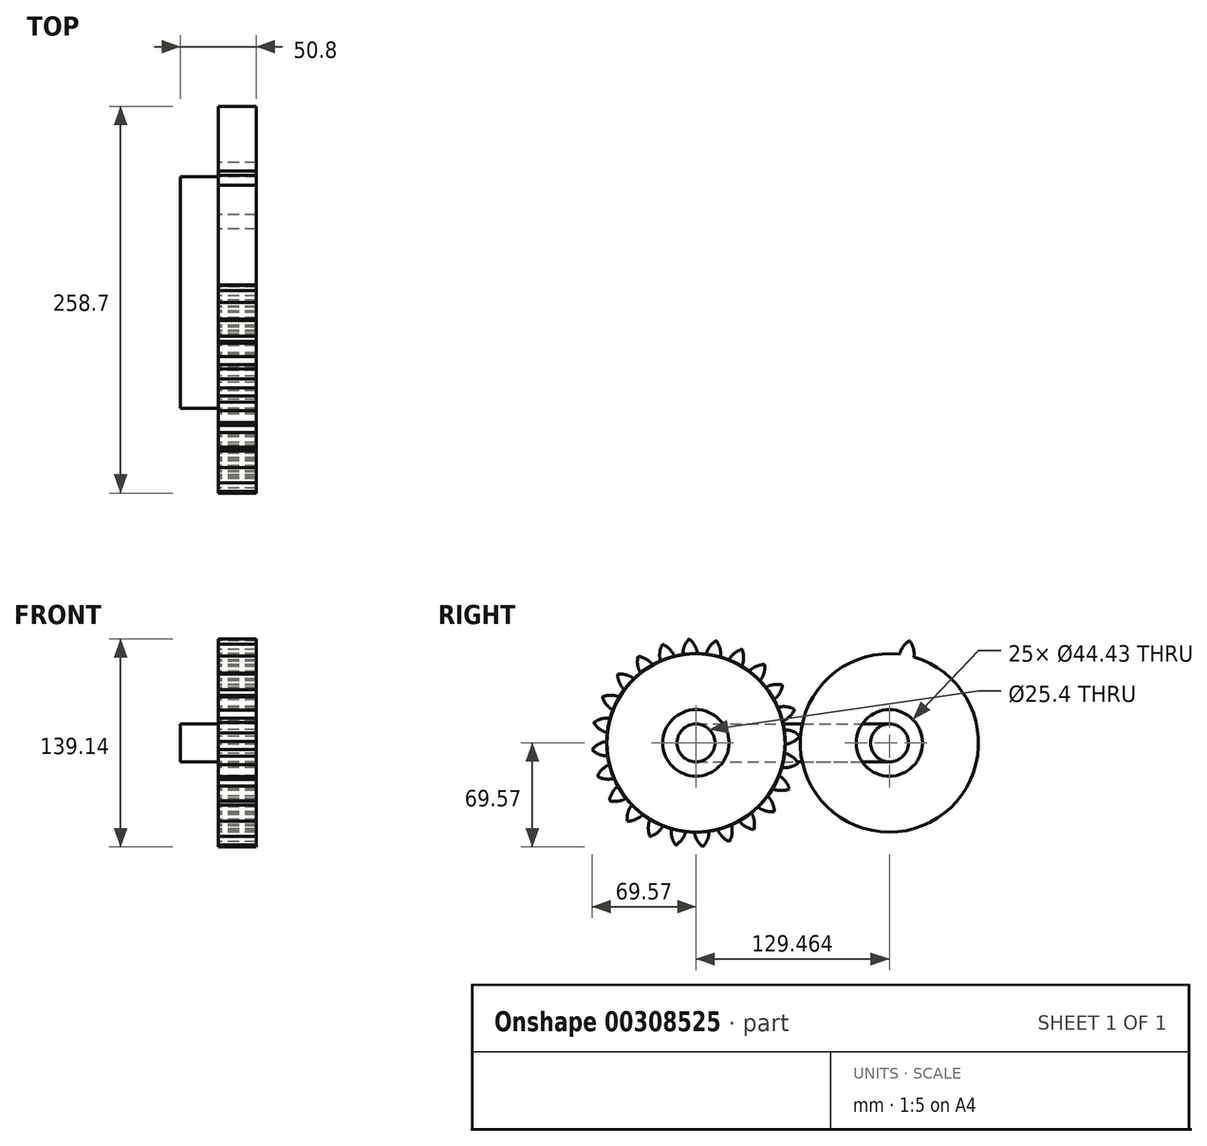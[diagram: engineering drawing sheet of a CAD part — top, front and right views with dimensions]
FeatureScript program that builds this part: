
annotation { "Feature Type Name" : "Feature", "Feature Type Description" : "" }
export const myFeature = defineFeature(function(context is Context, id is Id, definition is map)
    precondition{}
    {
        {
            var Q0;
            Q0=qCreatedBy(makeId("Right.planeOp"),FACE);
            var sketch = newSketch(context, id + "F0", { "sketchPlane" : qUnion([Q0])});
            skLineSegment(sketch, "E0.bottom", {"start": v(0, 0) * mm, "end": v(129.54, 0) * mm});
            skLineSegment(sketch, "E0.top", {"start": v(0, 25.4) * mm, "end": v(129.54, 25.4) * mm});
            skLineSegment(sketch, "E0.left", {"start": v(0, 0) * mm, "end": v(0, 25.4) * mm});
            skLineSegment(sketch, "E0.right", {"start": v(129.54, 0) * mm, "end": v(129.54, 25.4) * mm});
            skCircle(sketch, "E1", {"center": v(0, 12.7) * mm, "radius": 12.7 * mm});
            skCircle(sketch, "E2", {"center": v(129.54, 12.7) * mm, "radius": 12.7 * mm});
            skSolve(sketch);
        }
        {
            var Q0;
            Q0 = qSketchRegion(id + "F0", true);
            extrude(context, id + "F1", {"entities" : qUnion([Q0]), "depth" : 25.4 * mm});
        }
        {
            var Q0;
            {var subQ0=sQuery(id+"F0.wireOp",EDGE,"E0.left");Q0=makeQuery(id+"F0.imprint","IMPRINT",FACE,{"disambiguationData":[TD([[makeQuery(id+"F0.imprint","IMPRINT",EDGE,{"derivedFrom":subQ0}),1.0]])]});}
            var Q1;
            {var subQ0=sQuery(id+"F0.wireOp",EDGE,"E0.left");Q1=makeQuery(id+"F0.imprint","IMPRINT",FACE,{"disambiguationData":[TD([[makeQuery(id+"F0.imprint","IMPRINT",EDGE,{"derivedFrom":subQ0}),-1.0]])]});}
            var Q2;
            {var subQ0=sQuery(id+"F0.wireOp",EDGE,"E0.right");Q2=makeQuery(id+"F0.imprint","IMPRINT",FACE,{"disambiguationData":[TD([[makeQuery(id+"F0.imprint","IMPRINT",EDGE,{"derivedFrom":subQ0}),1.0]])]});}
            var Q3;
            {var subQ0=sQuery(id+"F0.wireOp",EDGE,"E0.right");Q3=makeQuery(id+"F0.imprint","IMPRINT",FACE,{"disambiguationData":[TD([[makeQuery(id+"F0.imprint","IMPRINT",EDGE,{"derivedFrom":subQ0}),-1.0]])]});}
            extrude(context, id + "F2", {"entities" : qUnion([Q0, Q1, Q2, Q3]), "operationType" : NewBodyOperationType.ADD, "depth" : 50.8 * mm});
        }
        {
            var Q0;
            Q0=makeQuery(id+"F2.opExtrude","CAP_FACE",FACE,{"disambiguationData":[OSD([sQuery(id+"F0.wireOp",EDGE,"E1")])],"isStart":false});
            var sketch = newSketch(context, id + "F3", { "sketchPlane" : qUnion([Q0])});
            skCircle(sketch, "E3", {"center": v(0, 12.7) * mm, "radius": 22.21 * mm});
            skCircle(sketch, "E4", {"center": v(0, 12.7) * mm, "radius": 53.72 * mm, "construction": true});
            skCircle(sketch, "E5", {"center": v(0, 12.7) * mm, "radius": 58.67 * mm, "construction": true});
            skCircle(sketch, "E6", {"center": v(0, 12.7) * mm, "radius": 63.5 * mm, "construction": true});
            skLineSegment(sketch, "E7", {"start": v(0, 12.7) * mm, "end": v(0, 90.96) * mm, "construction": true});
            skLineSegment(sketch, "E8", {"start": v(0, 12.7) * mm, "end": v(-5.27, 93.18) * mm, "construction": true});
            skLineSegment(sketch, "E9", {"start": v(0, 76.2) * mm, "end": v(-8.98, 76.2) * mm, "construction": true});
            skLineSegment(sketch, "E10", {"start": v(0, 76.2) * mm, "end": v(-51.07, 57.61) * mm, "construction": true});
            skCircle(sketch, "E11", {"center": v(0, 12.7) * mm, "radius": 59.67 * mm});
            skCircle(sketch, "E12", {"center": v(0, 76.2) * mm, "radius": 14.6 * mm, "construction": true});
            skCircle(sketch, "E13", {"center": v(-13.55, 70.76) * mm, "radius": 14.6 * mm, "construction": true});
            skArc(sketch, "E14", {"start": v(0, 76.2) * mm, "mid": v(-1.88, 79.53) * mm, "end": v(-4.56, 82.27) * mm});
            skArc(sketch, "E15", {"start": v(0.96, 72.36) * mm, "mid": v(0.62, 74.31) * mm, "end": v(0, 76.2) * mm});
            skArc(sketch, "E16.MirrorCS", {"start": v(-8.74, 71.73) * mm, "mid": v(-8.65, 73.7) * mm, "end": v(-8.29, 75.66) * mm});
            skArc(sketch, "E17.MirrorCS", {"start": v(-8.29, 75.66) * mm, "mid": v(-6.86, 79.2) * mm, "end": v(-4.56, 82.27) * mm});
            skSolve(sketch);
        }
        {
            var Q0;
            Q0 = qSketchRegion(id + "F3", true);
            extrude(context, id + "F4", {"entities" : qUnion([Q0]), "depth" : 25.4 * mm});
        }
        {
            var Q0;
            Q0=makeQuery(id+"F4.opExtrude","SWEPT_BODY",BODY,{"disambiguationData":[OSD([sQuery(id+"F3.wireOp",EDGE,"E3"),sQuery(id+"F3.wireOp",EDGE,"E11"),sQuery(id+"F3.wireOp",EDGE,"E14"),sQuery(id+"F3.wireOp",EDGE,"E15"),sQuery(id+"F3.wireOp",EDGE,"E16.MirrorCS"),sQuery(id+"F3.wireOp",EDGE,"E17.MirrorCS")])]});
            var Q1;
            Q1=makeQuery(id+"F4.opExtrude","SWEPT_FACE",FACE,{"disambiguationData":[OSD([sQuery(id+"F3.wireOp",EDGE,"E11")])]});
            circularPattern(context, id + "F5", {"entities" : qUnion([Q0]), "axis" : qUnion([Q1]), "angle" : 360 * degree, "instanceCount" : 24, "equalSpace" : true});
        }
        {
            var Q0;
            Q0=makeQuery(id+"F3.imprint","IMPRINT",FACE,{"disambiguationData":[TD([[makeQuery(id+"F3.imprint","IMPRINT",EDGE,{"derivedFrom":sQuery(id+"F3.wireOp",EDGE,"E3")}),1.0]])]});
            extrude(context, id + "F6", {"entities" : qUnion([Q0]), "depth" : 25.4 * mm});
        }
        {
            var Q0;
            Q0=makeQuery(id+"F1.opExtrude","SWEPT_BODY",BODY,{"disambiguationData":[OSD([sQuery(id+"F0.wireOp",EDGE,"E0.bottom"),sQuery(id+"F0.wireOp",EDGE,"E0.top"),sQuery(id+"F0.wireOp",EDGE,"E1"),sQuery(id+"F0.wireOp",EDGE,"E2")])]});
            transform(context, id + "F7", {"entities" : qUnion([Q0]), "transformType" : TransformType.TRANSLATION_3D, "dx" : 25.4 * mm, "dy" : 0 * mm, "dz" : 0 * mm, "makeCopy" : true});
        }
        {
            var Q0;
            Q0=makeQuery(id+"F1.opExtrude","SWEPT_BODY",BODY,{"disambiguationData":[OSD([sQuery(id+"F0.wireOp",EDGE,"E0.bottom"),sQuery(id+"F0.wireOp",EDGE,"E0.top"),sQuery(id+"F0.wireOp",EDGE,"E1"),sQuery(id+"F0.wireOp",EDGE,"E2")])]});
            deleteBodies(context, id + "F8", {"entities" : qUnion([Q0])});
        }
        {
            var Q0;
            Q0=makeQuery(id+"F5.opPattern","COPY",BODY,{"derivedFrom":makeQuery(id+"F4.opExtrude","SWEPT_BODY",BODY,{"disambiguationData":[OSD([sQuery(id+"F3.wireOp",EDGE,"E3"),sQuery(id+"F3.wireOp",EDGE,"E11"),sQuery(id+"F3.wireOp",EDGE,"E14"),sQuery(id+"F3.wireOp",EDGE,"E15"),sQuery(id+"F3.wireOp",EDGE,"E16.MirrorCS"),sQuery(id+"F3.wireOp",EDGE,"E17.MirrorCS")])]}),"instanceName":"1"});
            transform(context, id + "F9", {"entities" : qUnion([Q0]), "transformType" : TransformType.TRANSLATION_3D, "dx" : 0 * mm, "dy" : 129.46 * mm, "dz" : 0 * mm, "makeCopy" : true});
        }
    });
